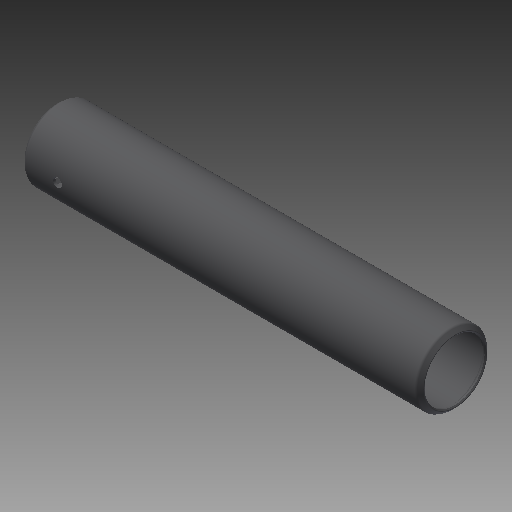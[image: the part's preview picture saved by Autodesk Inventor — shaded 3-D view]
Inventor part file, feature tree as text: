
AUTODESK INVENTOR PART (.ipt)
format: ipt  version: 2017 (Build 210142000, 142)  size: 155,136 bytes
history: native  units: in
note: dims shown in document units (in); Inventor stores cm internally (conversion verified against a paired STEP export)
features: other x42, sketch x2, revolve x1, extrude x1
ambient origin geometry x8: Origin, YZ Plane, XZ Plane, XY Plane, X Axis, Y Axis, Z Axis, Center Point
bodies: Solid1 (feature_tree)
feature tree (46):
  revolve  "Revolution1"  [1 undecoded]
  extrude  "Extrusion1"  [1 undecoded]
  other  "cp1_XY"
  other  "cp1_YZ"
  other  "cp1_ZX"
  other  "cp1_X"
  other  "cp1_Y"
  other  "cp1_Z"
  other  "cp1_Center"
  other  "cp2_XY"
  other  "cp2_YZ"
  other  "cp2_ZX"
  other  "cp2_X"
  other  "cp2_Y"
  other  "cp2_Z"
  other  "cp2_Center"
  other  "cp3_XY"
  other  "cp3_YZ"
  other  "cp3_ZX"
  other  "cp3_X"
  other  "cp3_Y"
  other  "cp3_Z"
  other  "cp3_Center"
  other  "cp4_XY"
  other  "cp4_YZ"
  other  "cp4_ZX"
  other  "cp4_X"
  other  "cp4_Y"
  other  "cp4_Z"
  other  "cp4_Center"
  other  "tube_front_XY"
  other  "tube_front_YZ"
  other  "tube_front_ZX"
  other  "tube_front_X"
  other  "tube_front_Y"
  other  "tube_front_Z"
  other  "tube_front_Center"
  other  "tube_rear_XY"
  other  "tube_rear_YZ"
  other  "tube_rear_ZX"
  other  "tube_rear_X"
  other  "tube_rear_Y"
  other  "tube_rear_Z"
  other  "tube_rear_Center"
  sketch  "Sketch_1"  dims[d0=360.0deg d1=0.242in d2=0.0in]
  sketch  "Sketch_4"
note: 2 required parameter values undecoded (feature->parameter linkage not recoverable at this tier; creation-order binding heuristic only, values carry confidence <= 0.55)